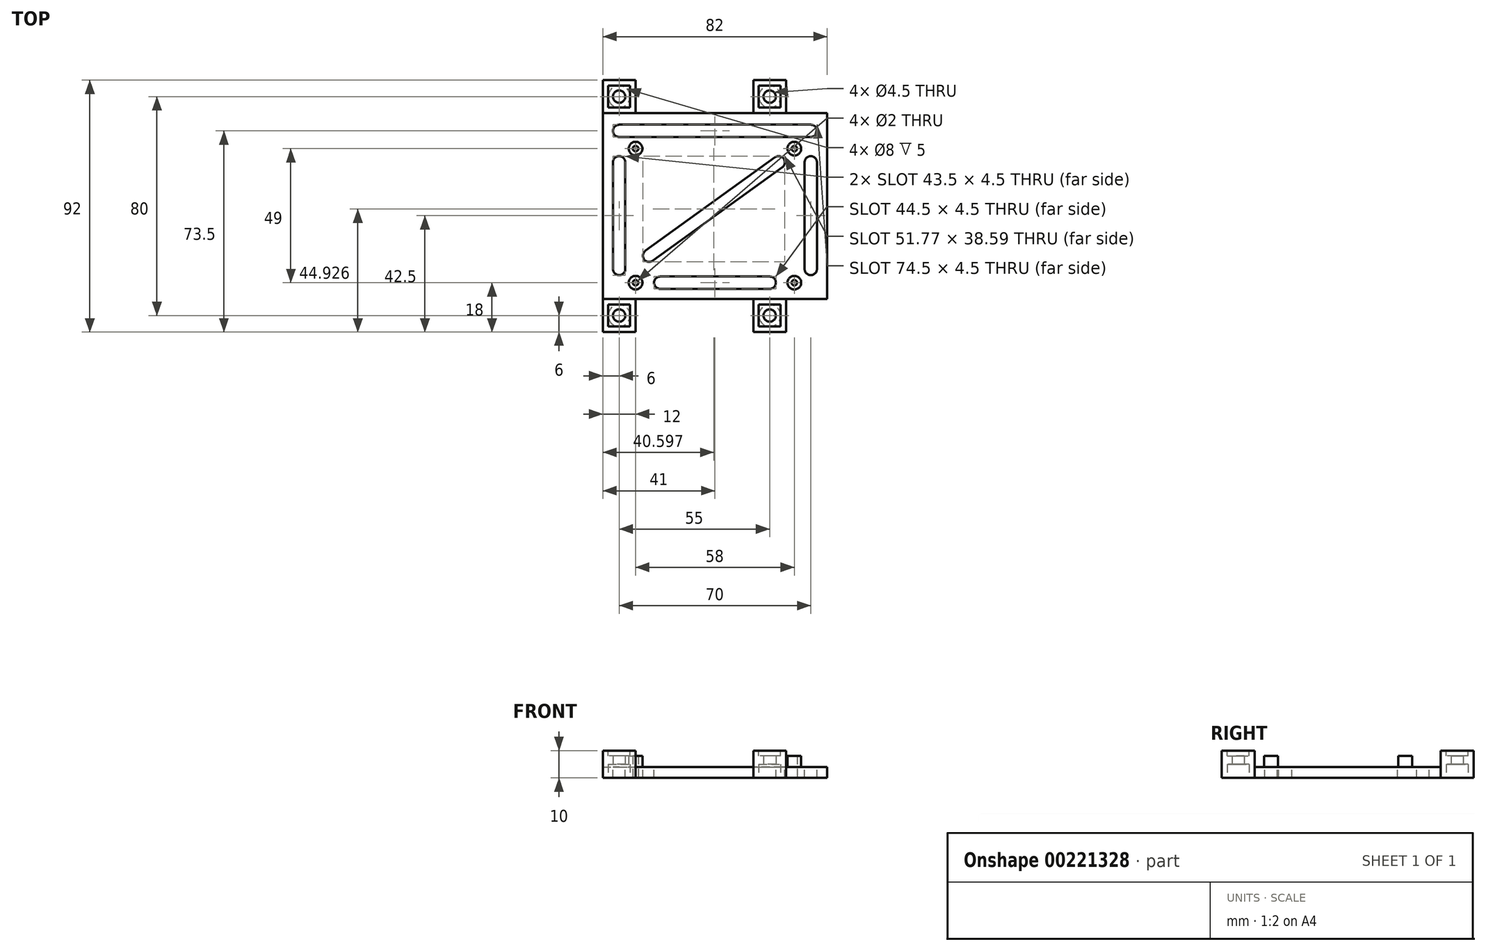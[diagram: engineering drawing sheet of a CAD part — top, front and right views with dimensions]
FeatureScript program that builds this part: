
annotation { "Feature Type Name" : "Feature", "Feature Type Description" : "" }
export const myFeature = defineFeature(function(context is Context, id is Id, definition is map)
    precondition{}
    {
        {
            var Q0;
            Q0=qCreatedBy(makeId("Top.planeOp"),FACE);
            var sketch = newSketch(context, id + "F0", { "sketchPlane" : qUnion([Q0])});
            skLineSegment(sketch, "E0", {"start": v(-42, 46) * mm, "end": v(-42, -46) * mm});
            skLineSegment(sketch, "E1", {"start": v(-42, -46) * mm, "end": v(-30, -46) * mm});
            skLineSegment(sketch, "E2", {"start": v(-30, -46) * mm, "end": v(-30, -34) * mm});
            skLineSegment(sketch, "E3", {"start": v(-30, -34) * mm, "end": v(13, -34) * mm});
            skLineSegment(sketch, "E4", {"start": v(13, -34) * mm, "end": v(13, -46) * mm});
            skLineSegment(sketch, "E5", {"start": v(13, -46) * mm, "end": v(25, -46) * mm});
            skLineSegment(sketch, "E6", {"start": v(25, -46) * mm, "end": v(25, -34) * mm});
            skLineSegment(sketch, "E7", {"start": v(25, -34) * mm, "end": v(40, -34) * mm});
            skLineSegment(sketch, "E8", {"start": v(40, -34) * mm, "end": v(40, 34) * mm});
            skLineSegment(sketch, "E9", {"start": v(40, 34) * mm, "end": v(25, 34) * mm});
            skLineSegment(sketch, "E10", {"start": v(25, 34) * mm, "end": v(25, 46) * mm});
            skLineSegment(sketch, "E11", {"start": v(25, 46) * mm, "end": v(13, 46) * mm});
            skLineSegment(sketch, "E12", {"start": v(13, 46) * mm, "end": v(13, 34) * mm});
            skLineSegment(sketch, "E13", {"start": v(13, 34) * mm, "end": v(-30, 34) * mm});
            skLineSegment(sketch, "E14", {"start": v(-30, 34) * mm, "end": v(-30, 46) * mm});
            skLineSegment(sketch, "E15", {"start": v(-30, 46) * mm, "end": v(-42, 46) * mm});
            skCircle(sketch, "E16", {"center": v(19, 40) * mm, "radius": 2.25 * mm});
            skPoint(sketch, "E16.centerSnap0", {"position": v(19, 46) * mm});
            skCircle(sketch, "E17", {"center": v(19, -40) * mm, "radius": 2.25 * mm});
            skPoint(sketch, "E17.centerSnap0", {"position": v(19, -46) * mm});
            skCircle(sketch, "E18", {"center": v(-36, -40) * mm, "radius": 2.25 * mm});
            skPoint(sketch, "E18.centerSnap0", {"position": v(-36, -46) * mm});
            skCircle(sketch, "E19", {"center": v(-36, 40) * mm, "radius": 2.25 * mm});
            skPoint(sketch, "E19.centerSnap0", {"position": v(-36, 46) * mm});
            skLineSegment(sketch, "E20", {"start": v(-36, -46) * mm, "end": v(-36, -40) * mm, "construction": true});
            skLineSegment(sketch, "E21", {"start": v(19, -46) * mm, "end": v(19, -40) * mm, "construction": true});
            skLineSegment(sketch, "E22", {"start": v(-36, 46) * mm, "end": v(-36, 40) * mm, "construction": true});
            skLineSegment(sketch, "E23", {"start": v(19, 46) * mm, "end": v(19, 40) * mm, "construction": true});
            skLineSegment(sketch, "E24", {"start": v(-30, 34) * mm, "end": v(0, 0) * mm, "construction": true});
            skLineSegment(sketch, "E25", {"start": v(0, 0) * mm, "end": v(-30, -34) * mm, "construction": true});
            skLineSegment(sketch, "E26.bottom", {"start": v(-30, 21) * mm, "end": v(28, 21) * mm, "construction": true});
            skLineSegment(sketch, "E26.top", {"start": v(-30, -28) * mm, "end": v(28, -28) * mm, "construction": true});
            skLineSegment(sketch, "E26.left", {"start": v(-30, 21) * mm, "end": v(-30, -28) * mm, "construction": true});
            skLineSegment(sketch, "E26.right", {"start": v(28, 21) * mm, "end": v(28, -28) * mm, "construction": true});
            skCircle(sketch, "E27", {"center": v(-30, 21) * mm, "radius": 1 * mm});
            skCircle(sketch, "E28", {"center": v(28, 21) * mm, "radius": 1 * mm});
            skCircle(sketch, "E29", {"center": v(28, -28) * mm, "radius": 1 * mm});
            skCircle(sketch, "E30", {"center": v(-30, -28) * mm, "radius": 1 * mm});
            skSolve(sketch);
        }
        {
            var Q0;
            Q0=makeQuery(id+"F0.imprint","IMPRINT",FACE,{"disambiguationData":[TD([[makeQuery(id+"F0.imprint","IMPRINT",EDGE,{"derivedFrom":sQuery(id+"F0.wireOp",EDGE,"E0")}),1.0]])]});
            extrude(context, id + "F1", {"entities" : qUnion([Q0]), "depth" : 4 * mm});
        }
        {
            var Q0;
            Q0=makeQuery(id+"F1.opExtrude","CAP_FACE",FACE,{"disambiguationData":[OSD([sQuery(id+"F0.wireOp",EDGE,"E0"),sQuery(id+"F0.wireOp",EDGE,"E1"),sQuery(id+"F0.wireOp",EDGE,"E2"),sQuery(id+"F0.wireOp",EDGE,"E3"),sQuery(id+"F0.wireOp",EDGE,"E4"),sQuery(id+"F0.wireOp",EDGE,"E5"),sQuery(id+"F0.wireOp",EDGE,"E6"),sQuery(id+"F0.wireOp",EDGE,"E7"),sQuery(id+"F0.wireOp",EDGE,"E8"),sQuery(id+"F0.wireOp",EDGE,"E9"),sQuery(id+"F0.wireOp",EDGE,"E10"),sQuery(id+"F0.wireOp",EDGE,"E11"),sQuery(id+"F0.wireOp",EDGE,"E12"),sQuery(id+"F0.wireOp",EDGE,"E13"),sQuery(id+"F0.wireOp",EDGE,"E14"),sQuery(id+"F0.wireOp",EDGE,"E15"),sQuery(id+"F0.wireOp",EDGE,"E16"),sQuery(id+"F0.wireOp",EDGE,"E17"),sQuery(id+"F0.wireOp",EDGE,"E18"),sQuery(id+"F0.wireOp",EDGE,"E19"),sQuery(id+"F0.wireOp",EDGE,"E27"),sQuery(id+"F0.wireOp",EDGE,"E28"),sQuery(id+"F0.wireOp",EDGE,"E29"),sQuery(id+"F0.wireOp",EDGE,"E30")])],"isStart":false});
            var sketch = newSketch(context, id + "F2", { "sketchPlane" : qUnion([Q0])});
            skLineSegment(sketch, "E31.bottom", {"start": v(-42, -46) * mm, "end": v(-30, -46) * mm});
            skLineSegment(sketch, "E31.top", {"start": v(-42, -34) * mm, "end": v(-30, -34) * mm});
            skLineSegment(sketch, "E31.left", {"start": v(-42, -46) * mm, "end": v(-42, -34) * mm});
            skLineSegment(sketch, "E31.right", {"start": v(-30, -46) * mm, "end": v(-30, -34) * mm});
            skLineSegment(sketch, "E32.bottom", {"start": v(-42, 46) * mm, "end": v(-30, 46) * mm});
            skLineSegment(sketch, "E32.top", {"start": v(-42, 34) * mm, "end": v(-30, 34) * mm});
            skLineSegment(sketch, "E32.left", {"start": v(-42, 46) * mm, "end": v(-42, 34) * mm});
            skLineSegment(sketch, "E32.right", {"start": v(-30, 46) * mm, "end": v(-30, 34) * mm});
            skLineSegment(sketch, "E33.bottom", {"start": v(13, 46) * mm, "end": v(25, 46) * mm});
            skLineSegment(sketch, "E33.top", {"start": v(13, 34) * mm, "end": v(25, 34) * mm});
            skLineSegment(sketch, "E33.left", {"start": v(13, 46) * mm, "end": v(13, 34) * mm});
            skLineSegment(sketch, "E33.right", {"start": v(25, 46) * mm, "end": v(25, 34) * mm});
            skLineSegment(sketch, "E34.bottom", {"start": v(13, -34) * mm, "end": v(25, -34) * mm});
            skLineSegment(sketch, "E34.top", {"start": v(13, -46) * mm, "end": v(25, -46) * mm});
            skLineSegment(sketch, "E34.left", {"start": v(13, -34) * mm, "end": v(13, -46) * mm});
            skLineSegment(sketch, "E34.right", {"start": v(25, -34) * mm, "end": v(25, -46) * mm});
            skSolve(sketch);
        }
        {
            var Q0;
            Q0=makeQuery(id+"F2.imprint","IMPRINT",FACE,{"disambiguationData":[TD([[makeQuery(id+"F2.imprint","IMPRINT",EDGE,{"derivedFrom":sQuery(id+"F2.wireOp",EDGE,"E31.bottom")}),1.0]])]});
            var Q1;
            Q1=makeQuery(id+"F2.imprint","IMPRINT",FACE,{"disambiguationData":[TD([[makeQuery(id+"F2.imprint","IMPRINT",EDGE,{"derivedFrom":sQuery(id+"F2.wireOp",EDGE,"E32.bottom")}),1.0]])]});
            var Q2;
            Q2=makeQuery(id+"F2.imprint","IMPRINT",FACE,{"disambiguationData":[TD([[makeQuery(id+"F2.imprint","IMPRINT",EDGE,{"derivedFrom":sQuery(id+"F2.wireOp",EDGE,"E33.bottom")}),1.0]])]});
            var Q3;
            Q3=makeQuery(id+"F2.imprint","IMPRINT",FACE,{"disambiguationData":[TD([[makeQuery(id+"F2.imprint","IMPRINT",EDGE,{"derivedFrom":sQuery(id+"F2.wireOp",EDGE,"E34.bottom")}),-1.0]])]});
            extrude(context, id + "F3", {"entities" : qUnion([Q0, Q1, Q2, Q3]), "operationType" : NewBodyOperationType.ADD, "depth" : 6 * mm});
        }
        {
            var Q0;
            Q0=makeQuery(id+"F3.opExtrude","CAP_FACE",FACE,{"disambiguationData":[OSD([sQuery(id+"F0.wireOp",EDGE,"E18"),sQuery(id+"F2.wireOp",EDGE,"E31.bottom"),sQuery(id+"F2.wireOp",EDGE,"E31.top"),sQuery(id+"F2.wireOp",EDGE,"E31.left"),sQuery(id+"F2.wireOp",EDGE,"E31.right")])],"isStart":false});
            var sketch = newSketch(context, id + "F4", { "sketchPlane" : qUnion([Q0])});
            skCircle(sketch, "E35.0", {"center": v(-36, 40) * mm, "radius": 2.25 * mm, "construction": true});
            skCircle(sketch, "E35.1", {"center": v(19, 40) * mm, "radius": 2.25 * mm, "construction": true});
            skCircle(sketch, "E35.2", {"center": v(19, -40) * mm, "radius": 2.25 * mm, "construction": true});
            skCircle(sketch, "E35.3", {"center": v(-36, -40) * mm, "radius": 2.25 * mm, "construction": true});
            skLineSegment(sketch, "E36.bottom", {"start": v(-32, 44) * mm, "end": v(-40, 44) * mm});
            skLineSegment(sketch, "E36.top", {"start": v(-32, 36) * mm, "end": v(-40, 36) * mm});
            skLineSegment(sketch, "E36.left", {"start": v(-32, 44) * mm, "end": v(-32, 36) * mm});
            skLineSegment(sketch, "E36.right", {"start": v(-40, 44) * mm, "end": v(-40, 36) * mm});
            skLineSegment(sketch, "E37.bottom", {"start": v(23, 44) * mm, "end": v(15, 44) * mm});
            skLineSegment(sketch, "E37.top", {"start": v(23, 36) * mm, "end": v(15, 36) * mm});
            skLineSegment(sketch, "E37.left", {"start": v(23, 44) * mm, "end": v(23, 36) * mm});
            skLineSegment(sketch, "E37.right", {"start": v(15, 44) * mm, "end": v(15, 36) * mm});
            skLineSegment(sketch, "E38.bottom", {"start": v(23, -44) * mm, "end": v(15, -44) * mm});
            skLineSegment(sketch, "E38.top", {"start": v(23, -36) * mm, "end": v(15, -36) * mm});
            skLineSegment(sketch, "E38.left", {"start": v(23, -44) * mm, "end": v(23, -36) * mm});
            skLineSegment(sketch, "E38.right", {"start": v(15, -44) * mm, "end": v(15, -36) * mm});
            skLineSegment(sketch, "E39.bottom", {"start": v(-40, -44) * mm, "end": v(-32, -44) * mm});
            skLineSegment(sketch, "E39.top", {"start": v(-40, -36) * mm, "end": v(-32, -36) * mm});
            skLineSegment(sketch, "E39.left", {"start": v(-40, -44) * mm, "end": v(-40, -36) * mm});
            skLineSegment(sketch, "E39.right", {"start": v(-32, -44) * mm, "end": v(-32, -36) * mm});
            skSolve(sketch);
        }
        {
            var Q0;
            Q0=makeQuery(id+"F4.imprint","IMPRINT",FACE,{"disambiguationData":[TD([[makeQuery(id+"F4.imprint","IMPRINT",EDGE,{"derivedFrom":sQuery(id+"F4.wireOp",EDGE,"E36.bottom")}),1.0]])]});
            var Q1;
            Q1=makeQuery(id+"F4.imprint","IMPRINT",FACE,{"disambiguationData":[TD([[makeQuery(id+"F4.imprint","IMPRINT",EDGE,{"derivedFrom":sQuery(id+"F4.wireOp",EDGE,"E37.bottom")}),1.0]])]});
            var Q2;
            Q2=makeQuery(id+"F4.imprint","IMPRINT",FACE,{"disambiguationData":[TD([[makeQuery(id+"F4.imprint","IMPRINT",EDGE,{"derivedFrom":sQuery(id+"F4.wireOp",EDGE,"E38.bottom")}),-1.0]])]});
            var Q3;
            Q3=makeQuery(id+"F4.imprint","IMPRINT",FACE,{"disambiguationData":[TD([[makeQuery(id+"F4.imprint","IMPRINT",EDGE,{"derivedFrom":sQuery(id+"F4.wireOp",EDGE,"E39.bottom")}),1.0]])]});
            extrude(context, id + "F5", {"entities" : qUnion([Q0, Q1, Q2, Q3]), "operationType" : NewBodyOperationType.REMOVE, "oppositeDirection" : true, "depth" : 2 * mm});
        }
        {
            var Q0;
            Q0=makeQuery(id+"F1.opExtrude","CAP_FACE",FACE,{"disambiguationData":[OSD([sQuery(id+"F0.wireOp",EDGE,"E0"),sQuery(id+"F0.wireOp",EDGE,"E1"),sQuery(id+"F0.wireOp",EDGE,"E2"),sQuery(id+"F0.wireOp",EDGE,"E3"),sQuery(id+"F0.wireOp",EDGE,"E4"),sQuery(id+"F0.wireOp",EDGE,"E5"),sQuery(id+"F0.wireOp",EDGE,"E6"),sQuery(id+"F0.wireOp",EDGE,"E7"),sQuery(id+"F0.wireOp",EDGE,"E8"),sQuery(id+"F0.wireOp",EDGE,"E9"),sQuery(id+"F0.wireOp",EDGE,"E10"),sQuery(id+"F0.wireOp",EDGE,"E11"),sQuery(id+"F0.wireOp",EDGE,"E12"),sQuery(id+"F0.wireOp",EDGE,"E13"),sQuery(id+"F0.wireOp",EDGE,"E14"),sQuery(id+"F0.wireOp",EDGE,"E15"),sQuery(id+"F0.wireOp",EDGE,"E16"),sQuery(id+"F0.wireOp",EDGE,"E17"),sQuery(id+"F0.wireOp",EDGE,"E18"),sQuery(id+"F0.wireOp",EDGE,"E19"),sQuery(id+"F0.wireOp",EDGE,"E27"),sQuery(id+"F0.wireOp",EDGE,"E28"),sQuery(id+"F0.wireOp",EDGE,"E29"),sQuery(id+"F0.wireOp",EDGE,"E30")])],"isStart":true});
            var sketch = newSketch(context, id + "F6", { "sketchPlane" : qUnion([Q0])});
            skCircle(sketch, "E40", {"center": v(-36, 40) * mm, "radius": 4 * mm});
            skCircle(sketch, "E41", {"center": v(19, 40) * mm, "radius": 4 * mm});
            skCircle(sketch, "E42", {"center": v(19, -40) * mm, "radius": 4 * mm});
            skCircle(sketch, "E43", {"center": v(-36, -40) * mm, "radius": 4 * mm});
            skSolve(sketch);
        }
        {
            var Q0;
            Q0=makeQuery(id+"F6.imprint","IMPRINT",FACE,{"disambiguationData":[TD([[makeQuery(id+"F6.imprint","IMPRINT",EDGE,{"derivedFrom":sQuery(id+"F6.wireOp",EDGE,"E40")}),1.0]])]});
            var Q1;
            Q1=makeQuery(id+"F6.imprint","IMPRINT",FACE,{"disambiguationData":[TD([[makeQuery(id+"F6.imprint","IMPRINT",EDGE,{"derivedFrom":sQuery(id+"F6.wireOp",EDGE,"E41")}),1.0]])]});
            var Q2;
            Q2=makeQuery(id+"F6.imprint","IMPRINT",FACE,{"disambiguationData":[TD([[makeQuery(id+"F6.imprint","IMPRINT",EDGE,{"derivedFrom":sQuery(id+"F6.wireOp",EDGE,"E42")}),1.0]])]});
            var Q3;
            Q3=makeQuery(id+"F6.imprint","IMPRINT",FACE,{"disambiguationData":[TD([[makeQuery(id+"F6.imprint","IMPRINT",EDGE,{"derivedFrom":sQuery(id+"F6.wireOp",EDGE,"E43")}),1.0]])]});
            extrude(context, id + "F7", {"entities" : qUnion([Q0, Q1, Q2, Q3]), "operationType" : NewBodyOperationType.REMOVE, "oppositeDirection" : true, "depth" : 5 * mm});
        }
        {
            var Q0;
            Q0=makeQuery(id+"F1.opExtrude","CAP_FACE",FACE,{"disambiguationData":[OSD([sQuery(id+"F0.wireOp",EDGE,"E0"),sQuery(id+"F0.wireOp",EDGE,"E1"),sQuery(id+"F0.wireOp",EDGE,"E2"),sQuery(id+"F0.wireOp",EDGE,"E3"),sQuery(id+"F0.wireOp",EDGE,"E4"),sQuery(id+"F0.wireOp",EDGE,"E5"),sQuery(id+"F0.wireOp",EDGE,"E6"),sQuery(id+"F0.wireOp",EDGE,"E7"),sQuery(id+"F0.wireOp",EDGE,"E8"),sQuery(id+"F0.wireOp",EDGE,"E9"),sQuery(id+"F0.wireOp",EDGE,"E10"),sQuery(id+"F0.wireOp",EDGE,"E11"),sQuery(id+"F0.wireOp",EDGE,"E12"),sQuery(id+"F0.wireOp",EDGE,"E13"),sQuery(id+"F0.wireOp",EDGE,"E14"),sQuery(id+"F0.wireOp",EDGE,"E15"),sQuery(id+"F0.wireOp",EDGE,"E16"),sQuery(id+"F0.wireOp",EDGE,"E17"),sQuery(id+"F0.wireOp",EDGE,"E18"),sQuery(id+"F0.wireOp",EDGE,"E19"),sQuery(id+"F0.wireOp",EDGE,"E27"),sQuery(id+"F0.wireOp",EDGE,"E28"),sQuery(id+"F0.wireOp",EDGE,"E29"),sQuery(id+"F0.wireOp",EDGE,"E30")])],"isStart":false});
            var sketch = newSketch(context, id + "F8", { "sketchPlane" : qUnion([Q0])});
            skCircle(sketch, "E44", {"center": v(-30, 21) * mm, "radius": 2.5 * mm});
            skCircle(sketch, "E45", {"center": v(-30, -28) * mm, "radius": 2.5 * mm});
            skCircle(sketch, "E46", {"center": v(28, 21) * mm, "radius": 2.5 * mm});
            skCircle(sketch, "E47", {"center": v(28, -28) * mm, "radius": 2.5 * mm});
            skSolve(sketch);
        }
        {
            var Q0;
            Q0=makeQuery(id+"F8.imprint","IMPRINT",FACE,{"disambiguationData":[TD([[makeQuery(id+"F8.imprint","IMPRINT",EDGE,{"derivedFrom":sQuery(id+"F8.wireOp",EDGE,"E44")}),1.0]])]});
            var Q1;
            Q1=makeQuery(id+"F8.imprint","IMPRINT",FACE,{"disambiguationData":[TD([[makeQuery(id+"F8.imprint","IMPRINT",EDGE,{"derivedFrom":sQuery(id+"F8.wireOp",EDGE,"E45")}),1.0]])]});
            var Q2;
            Q2=makeQuery(id+"F8.imprint","IMPRINT",FACE,{"disambiguationData":[TD([[makeQuery(id+"F8.imprint","IMPRINT",EDGE,{"derivedFrom":sQuery(id+"F8.wireOp",EDGE,"E47")}),1.0]])]});
            var Q3;
            Q3=makeQuery(id+"F8.imprint","IMPRINT",FACE,{"disambiguationData":[TD([[makeQuery(id+"F8.imprint","IMPRINT",EDGE,{"derivedFrom":sQuery(id+"F8.wireOp",EDGE,"E46")}),1.0]])]});
            extrude(context, id + "F9", {"entities" : qUnion([Q0, Q1, Q2, Q3]), "operationType" : NewBodyOperationType.ADD, "depth" : 4 * mm});
        }
        {
            var Q0;
            Q0=makeQuery(id+"F1.opExtrude","CAP_FACE",FACE,{"disambiguationData":[OSD([sQuery(id+"F0.wireOp",EDGE,"E0"),sQuery(id+"F0.wireOp",EDGE,"E1"),sQuery(id+"F0.wireOp",EDGE,"E2"),sQuery(id+"F0.wireOp",EDGE,"E3"),sQuery(id+"F0.wireOp",EDGE,"E4"),sQuery(id+"F0.wireOp",EDGE,"E5"),sQuery(id+"F0.wireOp",EDGE,"E6"),sQuery(id+"F0.wireOp",EDGE,"E7"),sQuery(id+"F0.wireOp",EDGE,"E8"),sQuery(id+"F0.wireOp",EDGE,"E9"),sQuery(id+"F0.wireOp",EDGE,"E10"),sQuery(id+"F0.wireOp",EDGE,"E11"),sQuery(id+"F0.wireOp",EDGE,"E12"),sQuery(id+"F0.wireOp",EDGE,"E13"),sQuery(id+"F0.wireOp",EDGE,"E14"),sQuery(id+"F0.wireOp",EDGE,"E15"),sQuery(id+"F0.wireOp",EDGE,"E16"),sQuery(id+"F0.wireOp",EDGE,"E17"),sQuery(id+"F0.wireOp",EDGE,"E18"),sQuery(id+"F0.wireOp",EDGE,"E19"),sQuery(id+"F0.wireOp",EDGE,"E27"),sQuery(id+"F0.wireOp",EDGE,"E28"),sQuery(id+"F0.wireOp",EDGE,"E29"),sQuery(id+"F0.wireOp",EDGE,"E30")])],"isStart":false});
            var sketch = newSketch(context, id + "F10", { "sketchPlane" : qUnion([Q0])});
            skCircle(sketch, "E48", {"center": v(-36, 27.5) * mm, "radius": 2.25 * mm});
            skCircle(sketch, "E49", {"center": v(34, 27.5) * mm, "radius": 2.25 * mm});
            skCircle(sketch, "E50", {"center": v(-36, 16) * mm, "radius": 2.25 * mm});
            skCircle(sketch, "E51", {"center": v(-36, -23) * mm, "radius": 2.25 * mm});
            skCircle(sketch, "E52", {"center": v(34, 16) * mm, "radius": 2.25 * mm});
            skCircle(sketch, "E53", {"center": v(34, -23) * mm, "radius": 2.25 * mm});
            skCircle(sketch, "E54", {"center": v(-21, -28) * mm, "radius": 2.25 * mm});
            skCircle(sketch, "E55", {"center": v(19, -28) * mm, "radius": 2.25 * mm});
            skLineSegment(sketch, "E56", {"start": v(-36, 29.75) * mm, "end": v(34, 29.75) * mm});
            skLineSegment(sketch, "E57", {"start": v(-36, 25.25) * mm, "end": v(34, 25.25) * mm});
            skLineSegment(sketch, "E58", {"start": v(-38.25, 16) * mm, "end": v(-38.25, -23) * mm});
            skLineSegment(sketch, "E59", {"start": v(-33.75, -23) * mm, "end": v(-33.75, 16) * mm});
            skLineSegment(sketch, "E60", {"start": v(31.75, 16) * mm, "end": v(31.75, -23) * mm});
            skLineSegment(sketch, "E61", {"start": v(36.25, -23) * mm, "end": v(36.25, 16) * mm});
            skLineSegment(sketch, "E62", {"start": v(19, -30.25) * mm, "end": v(-21, -30.25) * mm});
            skLineSegment(sketch, "E63", {"start": v(-21, -25.75) * mm, "end": v(19, -25.75) * mm});
            skLineSegment(sketch, "E64", {"start": v(-30, 21) * mm, "end": v(-30, 34) * mm, "construction": true});
            skLineSegment(sketch, "E65", {"start": v(-36, 27.5) * mm, "end": v(-30, 27.5) * mm, "construction": true});
            skLineSegment(sketch, "E66", {"start": v(-30, -28) * mm, "end": v(28, -28) * mm, "construction": true});
            skLineSegment(sketch, "E67", {"start": v(-36, 16) * mm, "end": v(34, 16) * mm, "construction": true});
            skLineSegment(sketch, "E68", {"start": v(-36, -23) * mm, "end": v(34, -23) * mm, "construction": true});
            skLineSegment(sketch, "E69", {"start": v(-36, 27.5) * mm, "end": v(-36, 16) * mm, "construction": true});
            skLineSegment(sketch, "E70", {"start": v(34, 27.5) * mm, "end": v(34, 16) * mm, "construction": true});
            skCircle(sketch, "E71", {"center": v(-25.07, -18.15) * mm, "radius": 2.25 * mm});
            skCircle(sketch, "E72", {"center": v(22.26, 16) * mm, "radius": 2.25 * mm});
            skLineSegment(sketch, "E73", {"start": v(-26.39, -16.32) * mm, "end": v(20.95, 17.82) * mm});
            skLineSegment(sketch, "E74", {"start": v(23.58, 14.18) * mm, "end": v(-23.75, -19.97) * mm});
            skSolve(sketch);
        }
        {
            var Q0;
            {var subQ0=sQuery(id+"F10.wireOp",EDGE,"E56");Q0=makeQuery(id+"F10.imprint","IMPRINT",FACE,{"disambiguationData":[TD([[makeQuery(id+"F10.imprint","IMPRINT",EDGE,{"derivedFrom":subQ0}),-1.0]])]});}
            var Q1;
            {var subQ0=sQuery(id+"F10.wireOp",EDGE,"E48");var subQ1=makeQuery(id+"F10.imprint","INTERSECT",VERTEX,{"derivedFrom":[subQ0,sQuery(id+"F10.wireOp",EDGE,"E56")]});Q1=makeQuery(id+"F10.imprint","IMPRINT",FACE,{"disambiguationData":[TD([[makeQuery(id+"F10.imprint","IMPRINT",EDGE,{"disambiguationData":[TD([[subQ1,-1.0]])],"derivedFrom":subQ0}),1.0]])]});}
            var Q2;
            {var subQ0=sQuery(id+"F10.wireOp",EDGE,"E50");var subQ1=makeQuery(id+"F10.imprint","INTERSECT",VERTEX,{"derivedFrom":[subQ0,sQuery(id+"F10.wireOp",EDGE,"E58")]});Q2=makeQuery(id+"F10.imprint","IMPRINT",FACE,{"disambiguationData":[TD([[makeQuery(id+"F10.imprint","IMPRINT",EDGE,{"disambiguationData":[TD([[subQ1,1.0]])],"derivedFrom":subQ0}),1.0]])]});}
            var Q3;
            {var subQ0=sQuery(id+"F10.wireOp",EDGE,"E58");Q3=makeQuery(id+"F10.imprint","IMPRINT",FACE,{"disambiguationData":[TD([[makeQuery(id+"F10.imprint","IMPRINT",EDGE,{"derivedFrom":subQ0}),1.0]])]});}
            var Q4;
            {var subQ0=sQuery(id+"F10.wireOp",EDGE,"E51");var subQ1=makeQuery(id+"F10.imprint","INTERSECT",VERTEX,{"derivedFrom":[subQ0,sQuery(id+"F10.wireOp",EDGE,"E58")]});Q4=makeQuery(id+"F10.imprint","IMPRINT",FACE,{"disambiguationData":[TD([[makeQuery(id+"F10.imprint","IMPRINT",EDGE,{"disambiguationData":[TD([[subQ1,1.0]])],"derivedFrom":subQ0}),1.0]])]});}
            var Q5;
            {var subQ0=sQuery(id+"F10.wireOp",EDGE,"E71");var subQ1=makeQuery(id+"F10.imprint","INTERSECT",VERTEX,{"derivedFrom":[subQ0,sQuery(id+"F10.wireOp",EDGE,"E73")]});Q5=makeQuery(id+"F10.imprint","IMPRINT",FACE,{"disambiguationData":[TD([[makeQuery(id+"F10.imprint","IMPRINT",EDGE,{"disambiguationData":[TD([[subQ1,-1.0]])],"derivedFrom":subQ0}),1.0]])]});}
            var Q6;
            {var subQ0=sQuery(id+"F10.wireOp",EDGE,"E73");Q6=makeQuery(id+"F10.imprint","IMPRINT",FACE,{"disambiguationData":[TD([[makeQuery(id+"F10.imprint","IMPRINT",EDGE,{"derivedFrom":subQ0}),-1.0]])]});}
            var Q7;
            {var subQ0=sQuery(id+"F10.wireOp",EDGE,"E72");var subQ1=makeQuery(id+"F10.imprint","INTERSECT",VERTEX,{"derivedFrom":[subQ0,sQuery(id+"F10.wireOp",EDGE,"E73")]});Q7=makeQuery(id+"F10.imprint","IMPRINT",FACE,{"disambiguationData":[TD([[makeQuery(id+"F10.imprint","IMPRINT",EDGE,{"disambiguationData":[TD([[subQ1,-1.0]])],"derivedFrom":subQ0}),1.0]])]});}
            var Q8;
            {var subQ0=sQuery(id+"F10.wireOp",EDGE,"E49");var subQ1=makeQuery(id+"F10.imprint","INTERSECT",VERTEX,{"derivedFrom":[subQ0,sQuery(id+"F10.wireOp",EDGE,"E56")]});Q8=makeQuery(id+"F10.imprint","IMPRINT",FACE,{"disambiguationData":[TD([[makeQuery(id+"F10.imprint","IMPRINT",EDGE,{"disambiguationData":[TD([[subQ1,-1.0]])],"derivedFrom":subQ0}),1.0]])]});}
            var Q9;
            {var subQ0=sQuery(id+"F10.wireOp",EDGE,"E60");Q9=makeQuery(id+"F10.imprint","IMPRINT",FACE,{"disambiguationData":[TD([[makeQuery(id+"F10.imprint","IMPRINT",EDGE,{"derivedFrom":subQ0}),1.0]])]});}
            var Q10;
            {var subQ0=sQuery(id+"F10.wireOp",EDGE,"E52");var subQ1=makeQuery(id+"F10.imprint","INTERSECT",VERTEX,{"derivedFrom":[subQ0,sQuery(id+"F10.wireOp",EDGE,"E60")]});Q10=makeQuery(id+"F10.imprint","IMPRINT",FACE,{"disambiguationData":[TD([[makeQuery(id+"F10.imprint","IMPRINT",EDGE,{"disambiguationData":[TD([[subQ1,1.0]])],"derivedFrom":subQ0}),1.0]])]});}
            var Q11;
            {var subQ0=sQuery(id+"F10.wireOp",EDGE,"E53");var subQ1=makeQuery(id+"F10.imprint","INTERSECT",VERTEX,{"derivedFrom":[subQ0,sQuery(id+"F10.wireOp",EDGE,"E60")]});Q11=makeQuery(id+"F10.imprint","IMPRINT",FACE,{"disambiguationData":[TD([[makeQuery(id+"F10.imprint","IMPRINT",EDGE,{"disambiguationData":[TD([[subQ1,1.0]])],"derivedFrom":subQ0}),1.0]])]});}
            var Q12;
            {var subQ0=sQuery(id+"F10.wireOp",EDGE,"E55");var subQ1=makeQuery(id+"F10.imprint","INTERSECT",VERTEX,{"derivedFrom":[subQ0,sQuery(id+"F10.wireOp",EDGE,"E62")]});Q12=makeQuery(id+"F10.imprint","IMPRINT",FACE,{"disambiguationData":[TD([[makeQuery(id+"F10.imprint","IMPRINT",EDGE,{"disambiguationData":[TD([[subQ1,1.0]])],"derivedFrom":subQ0}),1.0]])]});}
            var Q13;
            {var subQ0=sQuery(id+"F10.wireOp",EDGE,"E62");Q13=makeQuery(id+"F10.imprint","IMPRINT",FACE,{"disambiguationData":[TD([[makeQuery(id+"F10.imprint","IMPRINT",EDGE,{"derivedFrom":subQ0}),-1.0]])]});}
            var Q14;
            {var subQ0=sQuery(id+"F10.wireOp",EDGE,"E54");var subQ1=makeQuery(id+"F10.imprint","INTERSECT",VERTEX,{"derivedFrom":[subQ0,sQuery(id+"F10.wireOp",EDGE,"E62")]});Q14=makeQuery(id+"F10.imprint","IMPRINT",FACE,{"disambiguationData":[TD([[makeQuery(id+"F10.imprint","IMPRINT",EDGE,{"disambiguationData":[TD([[subQ1,1.0]])],"derivedFrom":subQ0}),1.0]])]});}
            extrude(context, id + "F11", {"entities" : qUnion([Q0, Q1, Q2, Q3, Q4, Q5, Q6, Q7, Q8, Q9, Q10, Q11, Q12, Q13, Q14]), "operationType" : NewBodyOperationType.REMOVE, "endBound" : BoundingType.THROUGH_ALL, "oppositeDirection" : true, "depth" : 25 * mm});
        }
    });
